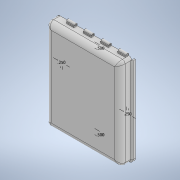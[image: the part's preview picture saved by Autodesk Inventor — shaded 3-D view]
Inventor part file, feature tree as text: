
AUTODESK INVENTOR PART (.ipt)
format: ipt  version: 2022 (Build 260153000, 153)  size: 312,832 bytes
history: native  units: in
note: dims shown in document units (in); Inventor stores cm internally (conversion verified against a paired STEP export)
features: sketch x12, extrude x11, plane x5, projected_geometry x4, fillet x3, chamfer x1
ambient origin geometry x8: Origin, YZ Plane, XZ Plane, XY Plane, X Axis, Y Axis, Z Axis, Center Point
bodies: Solid1 (feature_tree)
feature tree (36):
  extrude  "Extrusion1"  Depth=8.6in
  extrude  "Extrusion2"  Depth=0.125in TaperAngle=0.0deg
  fillet  "Fillet1"  Radius=0.125in
  fillet  "Fillet3"  Radius=0.125in
  fillet  "Fillet4"  Radius=0.5in
  sketch  "Sketch4"  dims[d13=0.25in d14=0.125in]
  sketch  "Sketch5"  dims[d17=0.5in d18=0.5in]
  plane  "Work Plane1"
  plane  "Work Plane2"
  plane  "Work Plane5"
  extrude  "Extrusion5"  Depth=0.125in
  sketch  "Sketch14"  dims[d21=0.25in d22=6.5in d23=1.625in]
  sketch  "Sketch15"  dims[d24=1.625in d25=1.625in d26=0.25in]
  sketch  "Sketch16"  dims[d27=0.25in d28=6.5in d29=0.0in]
  sketch  "Sketch17"  dims[d58=0.25in d59=0.25in]
  extrude  "Extrusion12"  Depth=0.5in
  extrude  "Extrusion13"  Depth=0.25in
  extrude  "Extrusion14"  Depth=0.25in
  extrude  "Extrusion15"  Depth=0.25in
  extrude  "Extrusion16"  Depth=0.25in TaperAngle=0.0deg
  extrude  "Extrusion17"  Depth=0.25in
  extrude  "Extrusion18"  Depth=0.25in
  extrude  "Extrusion21"  Depth=0.125in
  chamfer  "Chamfer2"  Distance=0.25in
  sketch  "Sketch1"  dims[d0=7.006in d1=8.6in]
  sketch  "Sketch2"  dims[d2=0.5in d3=1.11in d4=0.0in d5=0.125in d6=0.0in d10=0.125in d12=0.5in]
  projected_geometry  "Projected Loop1"
  plane  "Work Plane3"
  plane  "Work Plane4"
  sketch  "Sketch6"  dims[d19=0.25in d20=0.25in]
  sketch  "Sketch18"  dims[d60=0.125in d61=0.25in]
  sketch  "Sketch19"  dims[d62=0.25in d63=0.125in]
  projected_geometry  "Projected Loop7"
  projected_geometry  "Projected Loop8"
  projected_geometry  "Projected Loop9"
  sketch  "Sketch22"  dims[d64=0.25in d65=0.25in d66=0.125in d67=0.25in d68=0.25in d69=0.125in d70=0.7625in d71=0.0in d72=0.7625in d73=0.0in d74=0.7625in d75=0.0in d76=0.7625in d77=0.0in d78=0.2in d79=0.125in d80=5.5875in d81=0.0in d82=0.25in d83=0.0in d84=0.25in d85=0.0in d98=0.1in d99=0.0in d100=0.125in d101=0.125in d102=45.0deg d86=0.0in d87=0.0in]
